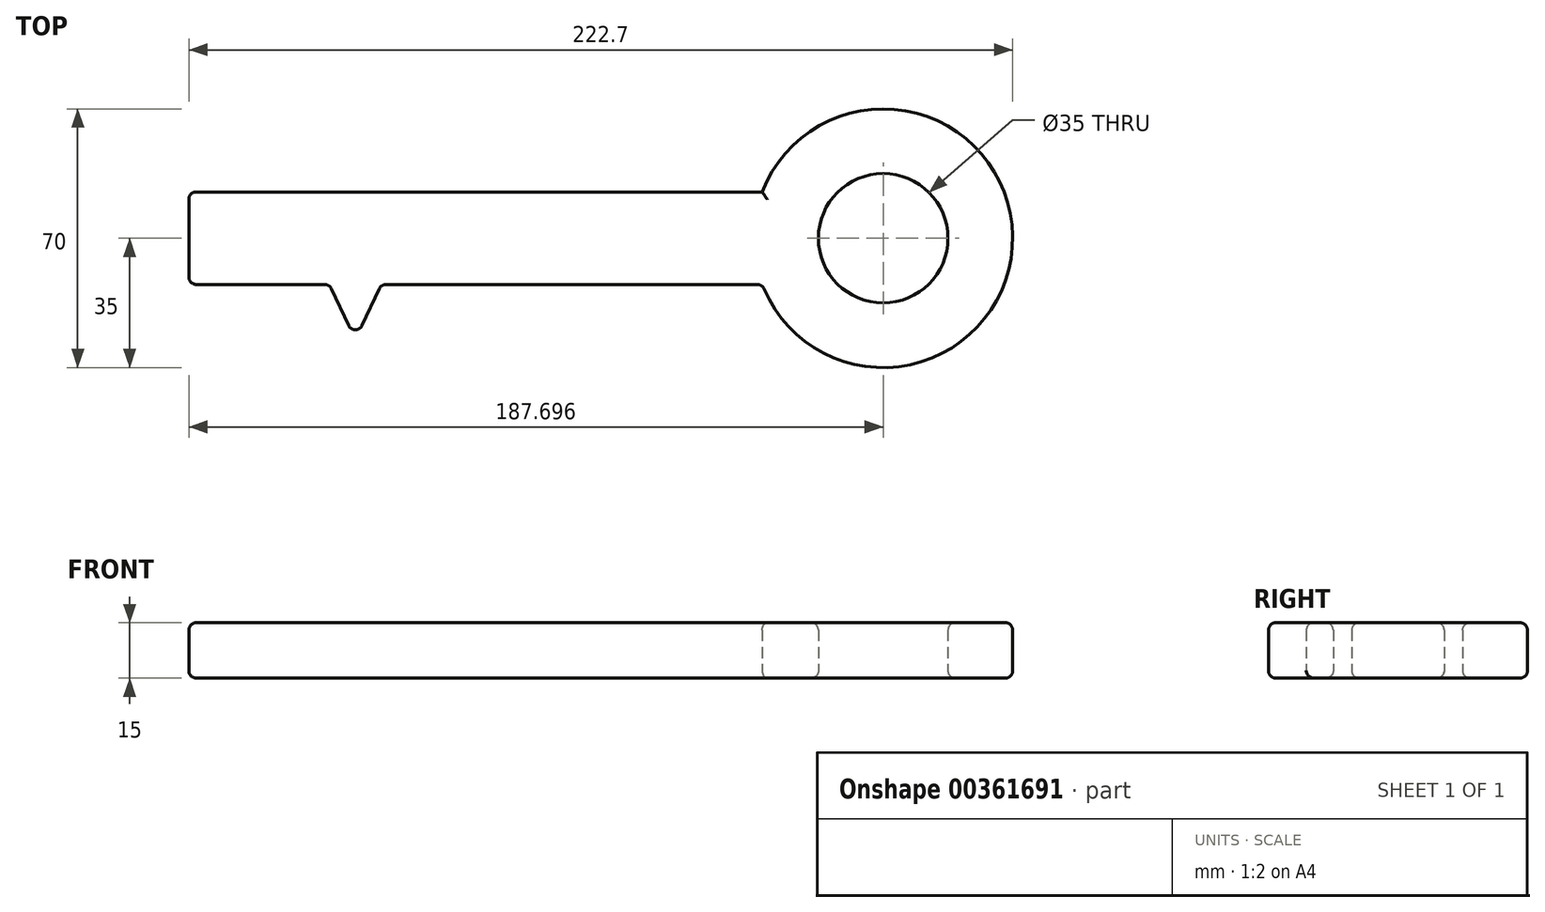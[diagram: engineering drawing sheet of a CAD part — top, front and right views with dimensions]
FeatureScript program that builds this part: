
annotation { "Feature Type Name" : "Feature", "Feature Type Description" : "" }
export const myFeature = defineFeature(function(context is Context, id is Id, definition is map)
    precondition{}
    {
        {
            var Q0;
            Q0=qCreatedBy(makeId("Top.planeOp"),FACE);
            var sketch = newSketch(context, id + "F0", { "sketchPlane" : qUnion([Q0])});
            skLineSegment(sketch, "E0.bottom", {"start": v(-158.28, 40) * mm, "end": v(-3.28, 40) * mm});
            skLineSegment(sketch, "E0.top", {"start": v(-158.28, 15) * mm, "end": v(-3.28, 15) * mm});
            skLineSegment(sketch, "E0.left", {"start": v(-158.28, 40) * mm, "end": v(-158.28, 15) * mm});
            skLineSegment(sketch, "E1.bottom", {"start": v(-138.28, 15) * mm, "end": v(-130.28, 15) * mm});
            skLineSegment(sketch, "E1.top", {"start": v(-138.28, 0) * mm, "end": v(-130.28, 0) * mm});
            skLineSegment(sketch, "E1.left", {"start": v(-138.28, 15) * mm, "end": v(-138.28, 0) * mm});
            skLineSegment(sketch, "E1.right", {"start": v(-130.28, 15) * mm, "end": v(-130.28, 0) * mm});
            skLineSegment(sketch, "E2", {"start": v(-120.28, 15) * mm, "end": v(-113.28, 0) * mm});
            skLineSegment(sketch, "E3", {"start": v(-113.28, 0) * mm, "end": v(-106.28, 15) * mm});
            skLineSegment(sketch, "E4.bottom", {"start": v(-158.28, 15) * mm, "end": v(-148.28, 15) * mm});
            skLineSegment(sketch, "E4.top", {"start": v(-158.28, -15) * mm, "end": v(-148.28, -15) * mm});
            skLineSegment(sketch, "E4.left", {"start": v(-158.28, 15) * mm, "end": v(-158.28, -15) * mm});
            skLineSegment(sketch, "E4.right", {"start": v(-148.28, 15) * mm, "end": v(-148.28, -15) * mm});
            skArc(sketch, "E5", {"start": v(-3.28, 15) * mm, "mid": v(64.42, 27.5) * mm, "end": v(-3.28, 40) * mm});
            skCircle(sketch, "E6", {"center": v(29.42, 27.5) * mm, "radius": 17.5 * mm});
            skLineSegment(sketch, "E7", {"start": v(29.42, 27.5) * mm, "end": v(-158.28, 27.5) * mm, "construction": true});
            skSolve(sketch);
        }
        {
            var Q0;
            {var subQ0=sQuery(id+"F0.wireOp",EDGE,"E2");Q0=makeQuery(id+"F0.imprint","IMPRINT",FACE,{"disambiguationData":[TD([[makeQuery(id+"F0.imprint","IMPRINT",EDGE,{"derivedFrom":subQ0}),1.0]])]});}
            var Q1;
            Q1=makeQuery(id+"F0.imprint","IMPRINT",FACE,{"disambiguationData":[TD([[makeQuery(id+"F0.imprint","IMPRINT",EDGE,{"derivedFrom":sQuery(id+"F0.wireOp",EDGE,"E1.bottom")}),-1.0]])]});
            var Q2;
            Q2=makeQuery(id+"F0.imprint","IMPRINT",FACE,{"disambiguationData":[TD([[makeQuery(id+"F0.imprint","IMPRINT",EDGE,{"derivedFrom":sQuery(id+"F0.wireOp",EDGE,"E4.bottom")}),-1.0]])]});
            var Q3;
            Q3=makeQuery(id+"F0.imprint","IMPRINT",FACE,{"disambiguationData":[TD([[makeQuery(id+"F0.imprint","IMPRINT",EDGE,{"derivedFrom":sQuery(id+"F0.wireOp",EDGE,"E0.bottom")}),-1.0]])]});
            extrude(context, id + "F1", {"entities" : qUnion([Q0, Q1, Q2, Q3]), "depth" : 15 * mm});
        }
        {
            var Q0;
            Q0=makeQuery(id+"F1.opExtrude","CAP_EDGE",EDGE,{"disambiguationData":[OSD([sQuery(id+"F0.wireOp",EDGE,"E0.bottom")])],"isStart":false});
            var Q1;
            {var subQ0=sQuery(id+"F0.wireOp",EDGE,"E0.top");Q1=makeQuery(id+"F1.opExtrude","CAP_EDGE",EDGE,{"disambiguationData":[OSD([subQ0]),TDD([makeQuery(id+"F0.imprint","IMPRINT",EDGE,{"disambiguationData":[TD([[makeQuery(id+"F0.imprint","INTERSECT",VERTEX,{"derivedFrom":[subQ0,sQuery(id+"F0.wireOp",EDGE,"E5")]}),1.0]])],"derivedFrom":subQ0})])],"isStart":false});}
            var Q2;
            Q2=makeQuery(id+"F1.opExtrude","CAP_EDGE",EDGE,{"disambiguationData":[OSD([sQuery(id+"F0.wireOp",EDGE,"E2")])],"isStart":false});
            var Q3;
            Q3=makeQuery(id+"F1.opExtrude","CAP_EDGE",EDGE,{"disambiguationData":[OSD([sQuery(id+"F0.wireOp",EDGE,"E3")])],"isStart":false});
            var Q4;
            Q4=makeQuery(id+"F1.opExtrude","CAP_EDGE",EDGE,{"disambiguationData":[OSD([sQuery(id+"F0.wireOp",EDGE,"E1.right")])],"isStart":false});
            var Q5;
            Q5=makeQuery(id+"F1.opExtrude","CAP_EDGE",EDGE,{"disambiguationData":[OSD([sQuery(id+"F0.wireOp",EDGE,"E1.top")])],"isStart":false});
            var Q6;
            {var subQ0=sQuery(id+"F0.wireOp",EDGE,"E0.top");Q6=makeQuery(id+"F1.opExtrude","CAP_EDGE",EDGE,{"disambiguationData":[OSD([subQ0]),TDD([makeQuery(id+"F0.imprint","IMPRINT",EDGE,{"disambiguationData":[TD([[makeQuery(id+"F0.imprint","INTERSECT",VERTEX,{"derivedFrom":[subQ0,sQuery(id+"F0.wireOp",EDGE,"E4.bottom"),sQuery(id+"F0.wireOp",EDGE,"E4.right")]}),-1.0]])],"derivedFrom":subQ0})])],"isStart":false});}
            var Q7;
            Q7=makeQuery(id+"F1.opExtrude","CAP_EDGE",EDGE,{"disambiguationData":[OSD([sQuery(id+"F0.wireOp",EDGE,"E1.left")])],"isStart":false});
            var Q8;
            Q8=makeQuery(id+"F1.opExtrude","CAP_EDGE",EDGE,{"disambiguationData":[OSD([sQuery(id+"F0.wireOp",EDGE,"E4.right")])],"isStart":false});
            var Q9;
            Q9=makeQuery(id+"F1.opExtrude","CAP_EDGE",EDGE,{"disambiguationData":[OSD([sQuery(id+"F0.wireOp",EDGE,"E4.top")])],"isStart":false});
            var Q10;
            Q10=makeQuery(id+"F1.opExtrude","CAP_EDGE",EDGE,{"disambiguationData":[OSD([sQuery(id+"F0.wireOp",EDGE,"E0.left"),sQuery(id+"F0.wireOp",EDGE,"E4.left")])],"isStart":false});
            var Q11;
            Q11=makeQuery(id+"F1.opExtrude","CAP_EDGE",EDGE,{"disambiguationData":[OSD([sQuery(id+"F0.wireOp",EDGE,"E5")])],"isStart":false});
            var Q12;
            Q12=makeQuery(id+"F1.opExtrude","CAP_EDGE",EDGE,{"disambiguationData":[OSD([sQuery(id+"F0.wireOp",EDGE,"E6")])],"isStart":false});
            var Q13;
            {var subQ0=sQuery(id+"F0.wireOp",EDGE,"E0.top");Q13=makeQuery(id+"F1.opExtrude","SWEPT_FACE",FACE,{"disambiguationData":[OSD([subQ0]),TDD([makeQuery(id+"F0.imprint","IMPRINT",EDGE,{"disambiguationData":[TD([[makeQuery(id+"F0.imprint","INTERSECT",VERTEX,{"derivedFrom":[subQ0,sQuery(id+"F0.wireOp",EDGE,"E5")]}),1.0]])],"derivedFrom":subQ0})])]});}
            var Q14;
            Q14=makeQuery(id+"F1.opExtrude","CAP_EDGE",EDGE,{"disambiguationData":[OSD([sQuery(id+"F0.wireOp",EDGE,"E3")])],"isStart":true});
            var Q15;
            Q15=makeQuery(id+"F1.opExtrude","SWEPT_EDGE",EDGE,{"disambiguationData":[OSD([sQuery(id+"F0.wireOp",EDGE,"E2"),sQuery(id+"F0.wireOp",EDGE,"E3")])]});
            var Q16;
            Q16=makeQuery(id+"F1.opExtrude","CAP_EDGE",EDGE,{"disambiguationData":[OSD([sQuery(id+"F0.wireOp",EDGE,"E2")])],"isStart":true});
            var Q17;
            Q17=makeQuery(id+"F1.opExtrude","SWEPT_EDGE",EDGE,{"disambiguationData":[OSD([sQuery(id+"F0.wireOp",EDGE,"E0.top"),sQuery(id+"F0.wireOp",EDGE,"E2")])]});
            var Q18;
            Q18=makeQuery(id+"F1.opExtrude","CAP_EDGE",EDGE,{"disambiguationData":[OSD([sQuery(id+"F0.wireOp",EDGE,"E1.top")])],"isStart":true});
            var Q19;
            Q19=makeQuery(id+"F1.opExtrude","SWEPT_EDGE",EDGE,{"disambiguationData":[OSD([sQuery(id+"F0.wireOp",EDGE,"E1.top"),sQuery(id+"F0.wireOp",EDGE,"E1.right")])]});
            var Q20;
            Q20=makeQuery(id+"F1.opExtrude","SWEPT_EDGE",EDGE,{"disambiguationData":[OSD([sQuery(id+"F0.wireOp",EDGE,"E1.top"),sQuery(id+"F0.wireOp",EDGE,"E1.left")])]});
            var Q21;
            Q21=makeQuery(id+"F1.opExtrude","SWEPT_FACE",FACE,{"disambiguationData":[OSD([sQuery(id+"F0.wireOp",EDGE,"E4.top")])]});
            var Q22;
            Q22=makeQuery(id+"F1.opExtrude","SWEPT_EDGE",EDGE,{"disambiguationData":[OSD([sQuery(id+"F0.wireOp",EDGE,"E4.top"),sQuery(id+"F0.wireOp",EDGE,"E4.left")])]});
            var Q23;
            Q23=makeQuery(id+"F1.opExtrude","SWEPT_EDGE",EDGE,{"disambiguationData":[OSD([sQuery(id+"F0.wireOp",EDGE,"E4.top"),sQuery(id+"F0.wireOp",EDGE,"E4.right")])]});
            var Q24;
            Q24=makeQuery(id+"F1.opExtrude","SWEPT_EDGE",EDGE,{"disambiguationData":[OSD([sQuery(id+"F0.wireOp",EDGE,"E0.bottom"),sQuery(id+"F0.wireOp",EDGE,"E0.left")])]});
            var Q25;
            Q25=makeQuery(id+"F1.opExtrude","CAP_EDGE",EDGE,{"disambiguationData":[OSD([sQuery(id+"F0.wireOp",EDGE,"E0.left"),sQuery(id+"F0.wireOp",EDGE,"E4.left")])],"isStart":true});
            var Q26;
            Q26=makeQuery(id+"F1.opExtrude","CAP_EDGE",EDGE,{"disambiguationData":[OSD([sQuery(id+"F0.wireOp",EDGE,"E0.bottom")])],"isStart":true});
            var Q27;
            Q27=makeQuery(id+"F1.opExtrude","CAP_EDGE",EDGE,{"disambiguationData":[OSD([sQuery(id+"F0.wireOp",EDGE,"E5")])],"isStart":true});
            var Q28;
            Q28=makeQuery(id+"F1.opExtrude","SWEPT_FACE",FACE,{"disambiguationData":[OSD([sQuery(id+"F0.wireOp",EDGE,"E6")])]});
            var Q29;
            {var subQ0=sQuery(id+"F0.wireOp",EDGE,"E0.top");Q29=makeQuery(id+"F1.opExtrude","CAP_EDGE",EDGE,{"disambiguationData":[OSD([subQ0]),TDD([makeQuery(id+"F0.imprint","IMPRINT",EDGE,{"disambiguationData":[TD([[makeQuery(id+"F0.imprint","INTERSECT",VERTEX,{"derivedFrom":[subQ0,sQuery(id+"F0.wireOp",EDGE,"E2")]}),1.0]])],"derivedFrom":subQ0})])],"isStart":true});}
            var Q30;
            Q30=makeQuery(id+"F1.opExtrude","SWEPT_EDGE",EDGE,{"disambiguationData":[OSD([sQuery(id+"F0.wireOp",EDGE,"E0.top"),sQuery(id+"F0.wireOp",EDGE,"E1.bottom"),sQuery(id+"F0.wireOp",EDGE,"E1.right")])]});
            var Q31;
            Q31=makeQuery(id+"F1.opExtrude","SWEPT_EDGE",EDGE,{"disambiguationData":[OSD([sQuery(id+"F0.wireOp",EDGE,"E0.top"),sQuery(id+"F0.wireOp",EDGE,"E3")])]});
            var Q32;
            {var subQ0=sQuery(id+"F0.wireOp",EDGE,"E0.top");Q32=makeQuery(id+"F1.opExtrude","CAP_EDGE",EDGE,{"disambiguationData":[OSD([subQ0]),TDD([makeQuery(id+"F0.imprint","IMPRINT",EDGE,{"disambiguationData":[TD([[makeQuery(id+"F0.imprint","INTERSECT",VERTEX,{"derivedFrom":[subQ0,sQuery(id+"F0.wireOp",EDGE,"E2")]}),1.0]])],"derivedFrom":subQ0})])],"isStart":false});}
            fillet(context, id + "F2", {"entities" : qUnion([Q0, Q1, Q2, Q3, Q4, Q5, Q6, Q7, Q8, Q9, Q10, Q11, Q12, Q13, Q14, Q15, Q16, Q17, Q18, Q19, Q20, Q21, Q22, Q23, Q24, Q25, Q26, Q27, Q28, Q29, Q30, Q31, Q32]), "radius" : 2 * mm, "tangentPropagation" : true, "allowEdgeOverflow" : false});
        }
    });
